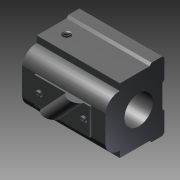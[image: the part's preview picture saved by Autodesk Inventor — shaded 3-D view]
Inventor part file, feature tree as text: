
AUTODESK INVENTOR PART (.ipt)
format: ipt  version: 2016 (Build 200138000, 138)  size: 220,672 bytes
history: native  units: mm
features: sketch x9, other x7, extrude x5, revolve x2, hole x2, pattern_linear x1
ambient origin geometry x8: Origin, YZ Plane, XZ Plane, XY Plane, X Axis, Y Axis, Z Axis, Center Point
bodies: Solid1 (feature_tree)
feature tree (26):
  extrude  "Extrusion1"  Depth=58.0mm TaperAngle=0.0deg
  extrude  "Extrusion2"  TaperAngle=360.0deg  [1 undecoded]
  extrude  "Extrusion3"  Depth=0.8mm TaperAngle=0.0deg
  revolve  "Revolution1"  [1 undecoded]
  revolve  "Revolution2"  [1 undecoded]
  extrude  "Extrusion4"  [1 undecoded]
  extrude  "Extrusion5"  [1 undecoded]
  hole  "Hole1"  [1 undecoded]
  hole  "Hole2"  [1 undecoded]
  pattern_linear  "Rectangular Pattern1"  [2 undecoded]
  other  "bnt_nut_1_XY"
  other  "bnt_nut_1_YZ"
  other  "bnt_nut_1_ZX"
  other  "bnt_nut_1_X"
  other  "bnt_nut_1_Y"
  other  "bnt_nut_1_Z"
  other  "bnt_nut_1_Center"
  sketch  "Sketch_1"  dims[d0=58.0mm d1=0.0mm d2=58.0mm d3=0.0mm]
  sketch  "Sketch_2"  dims[d4=4.6mm d5=0.0mm d6=360.0deg]
  sketch  "Sketch_3"  dims[d7=360.0deg d8=0.8mm d9=0.0mm]
  sketch  "Sketch_4"  dims[d10=0.8mm d11=0.0mm]
  sketch  "Sketch_5"  dims[d12=4.917mm d13=10.5415mm d14=6.0mm d15=2.0mm d16=90.0deg d17=14.140584mm d18=120.0deg]
  sketch  "Sketch_6"  dims[d19=4.917mm d20=10.5415mm d21=6.0mm d22=2.0mm d23=90.0deg d24=13.140584mm d25=120.0deg d26=20.0mm d28=35.0mm d29=20.0mm d31=35.0mm]
  sketch  "Sketch_7"  dims[d32=0.0mm]
  sketch  "Sketch8"
  sketch  "Sketch9"
note: 9 required parameter values undecoded (feature->parameter linkage not recoverable at this tier; creation-order binding heuristic only, values carry confidence <= 0.55)